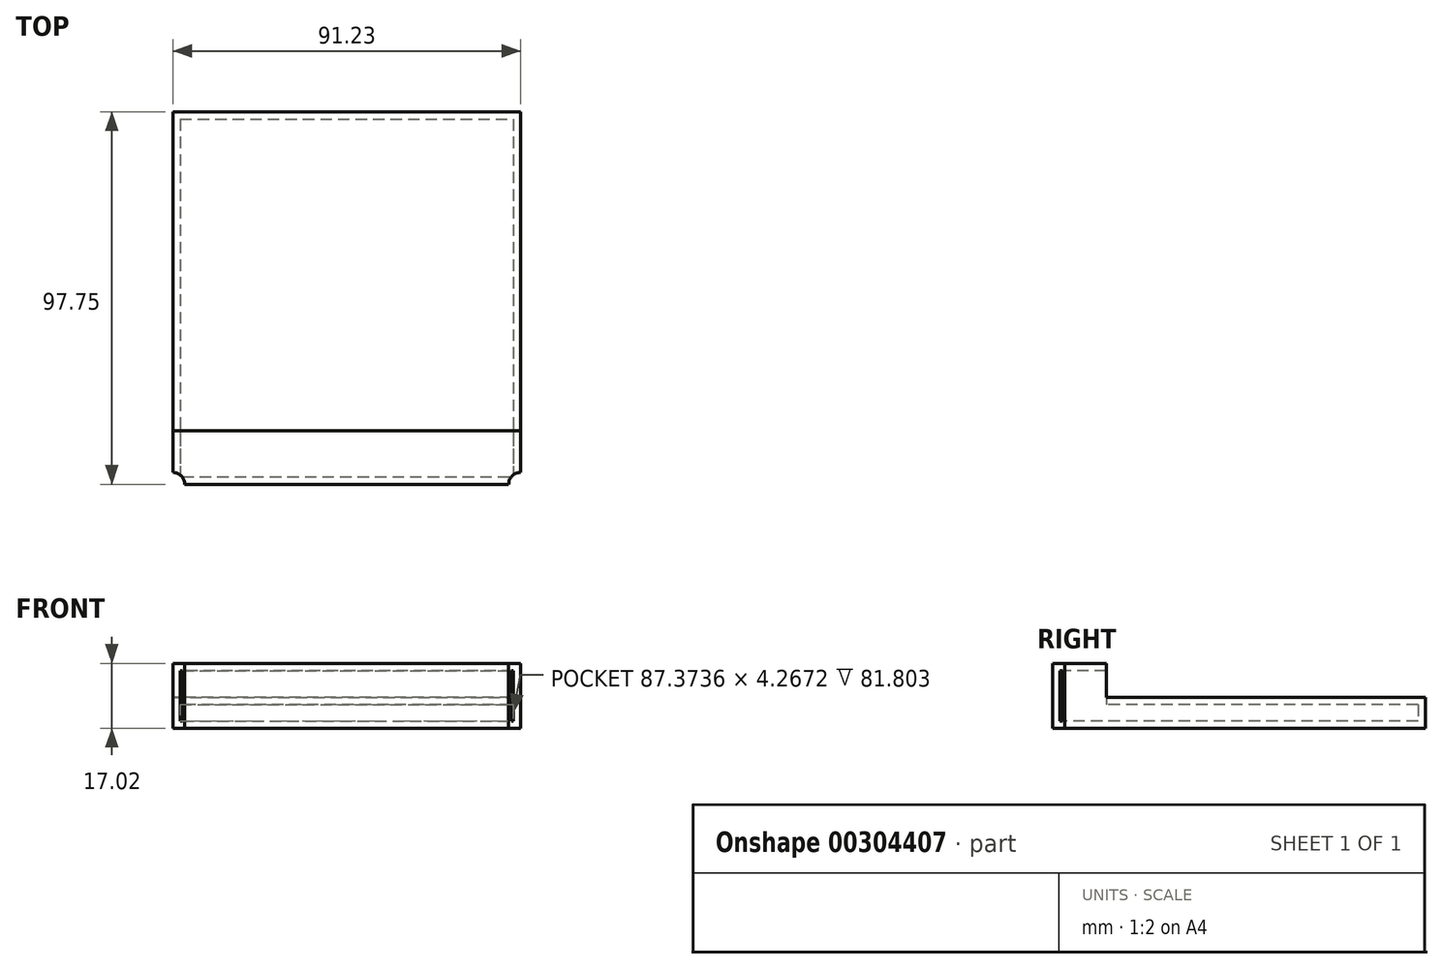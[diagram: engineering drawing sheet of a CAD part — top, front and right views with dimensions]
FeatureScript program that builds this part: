
annotation { "Feature Type Name" : "Feature", "Feature Type Description" : "" }
export const myFeature = defineFeature(function(context is Context, id is Id, definition is map)
    precondition{}
    {
        {
            var Q0;
            Q0=qCreatedBy(makeId("Top.planeOp"),FACE);
            var sketch = newSketch(context, id + "F0", { "sketchPlane" : qUnion([Q0])});
            skLineSegment(sketch, "E0", {"start": v(-63.03, 51.41) * mm, "end": v(45.76, 51.41) * mm});
            skLineSegment(sketch, "E1", {"start": v(45.76, 51.41) * mm, "end": v(45.76, -32.32) * mm});
            skLineSegment(sketch, "E2", {"start": v(45.76, -32.32) * mm, "end": v(-63.03, -32.32) * mm});
            skLineSegment(sketch, "E3", {"start": v(-63.03, -32.32) * mm, "end": v(-63.03, 51.41) * mm});
            skLineSegment(sketch, "E4", {"start": v(-53.82, 51.41) * mm, "end": v(-53.82, -46.34) * mm});
            skLineSegment(sketch, "E5", {"start": v(-63.03, -46.34) * mm, "end": v(-63.03, -32.32) * mm});
            skLineSegment(sketch, "E6", {"start": v(-63.03, -46.34) * mm, "end": v(-53.82, -46.34) * mm});
            skLineSegment(sketch, "E7", {"start": v(-53.82, -46.34) * mm, "end": v(45.76, -46.34) * mm});
            skLineSegment(sketch, "E8", {"start": v(45.76, -32.32) * mm, "end": v(45.76, -46.34) * mm});
            skLineSegment(sketch, "E9", {"start": v(37.41, 51.41) * mm, "end": v(37.41, -46.34) * mm});
            skSolve(sketch);
        }
        {
            var Q0;
            {var subQ0=sQuery(id+"F0.wireOp",EDGE,"E4");var subQ1=sQuery(id+"F0.wireOp",EDGE,"E0");var subQ2=makeQuery(id+"F0.imprint","INTERSECT",VERTEX,{"derivedFrom":[subQ1,subQ0]});Q0=makeQuery(id+"F0.imprint","IMPRINT",FACE,{"disambiguationData":[TD([[makeQuery(id+"F0.imprint","IMPRINT",EDGE,{"disambiguationData":[TD([[subQ2,-1.0]])],"derivedFrom":subQ1}),-1.0]])]});}
            extrude(context, id + "F1", {"entities" : qUnion([Q0]), "depth" : 8.13 * mm});
        }
        {
            var Q0;
            {var subQ0=sQuery(id+"F0.wireOp",EDGE,"E9");var subQ1=sQuery(id+"F0.wireOp",EDGE,"E2");var subQ2=makeQuery(id+"F0.imprint","INTERSECT",VERTEX,{"derivedFrom":[subQ1,subQ0]});Q0=makeQuery(id+"F0.imprint","IMPRINT",FACE,{"disambiguationData":[TD([[makeQuery(id+"F0.imprint","IMPRINT",EDGE,{"disambiguationData":[TD([[subQ2,-1.0]])],"derivedFrom":subQ1}),1.0]])]});}
            extrude(context, id + "F2", {"entities" : qUnion([Q0]), "operationType" : NewBodyOperationType.ADD, "depth" : 17.02 * mm});
        }
        {
            var Q0;
            Q0=makeQuery(id+"F2.opExtrude","SWEPT_FACE",FACE,{"disambiguationData":[OSD([sQuery(id+"F0.wireOp",EDGE,"E2")])]});
            shell(context, id + "F3", {"entities" : qUnion([Q0]), "thickness" : 1.93 * mm});
        }
        {
            var Q0;
            Q0=sQuery(id+"F0.wireOp",VERTEX,"E9.end");
            var Q1;
            Q1=sQuery(id+"F0.wireOp",VERTEX,"E7.start");
            var Q2;
            Q2=makeQuery(id+"F1.opExtrude","SWEPT_BODY",BODY,{"disambiguationData":[OSD([sQuery(id+"F0.wireOp",EDGE,"E0"),sQuery(id+"F0.wireOp",EDGE,"E2"),sQuery(id+"F0.wireOp",EDGE,"E4"),sQuery(id+"F0.wireOp",EDGE,"E9")])]});
            hole(context, id + "F4", {"style" : HoleStyle.SIMPLE, "endStyle" : HoleEndStyle.THROUGH, "oppositeDirection" : true, "standardTappedOrClearance" : lookupTablePath({ "standard" : "ANSI", "size" : "D (0.25)", "type" : "Drilled" }), "standardBlindInLast" : lookupTablePath({ "standard" : "ANSI", "size" : "D", "type" : "Drilled" }), "holeDiameter" : 6.25 * mm, "tappedDepth" : 12.7 * mm, "tapClearance" : 3, "locations" : qUnion([Q0, Q1]), "scope" : qUnion([Q2])});
        }
    });
